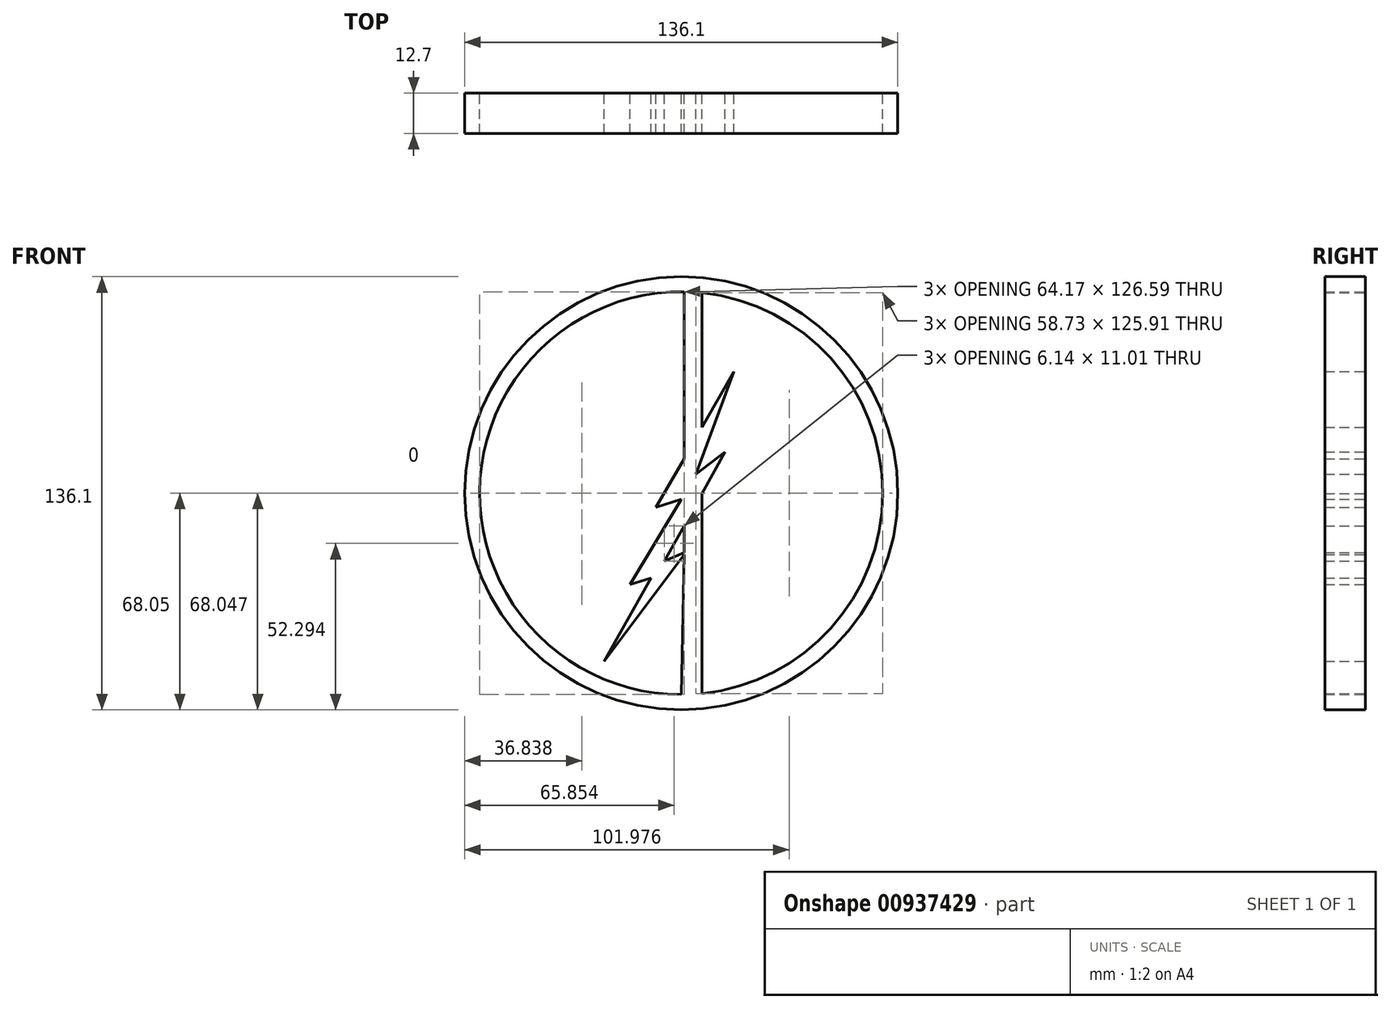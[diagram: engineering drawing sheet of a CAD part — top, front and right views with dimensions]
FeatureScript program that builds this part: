
annotation { "Feature Type Name" : "Feature", "Feature Type Description" : "" }
export const myFeature = defineFeature(function(context is Context, id is Id, definition is map)
    precondition{}
    {
        {
            var Q0;
            Q0=qCreatedBy(makeId("Front.planeOp"),FACE);
            var sketch = newSketch(context, id + "F0", { "sketchPlane" : qUnion([Q0])});
            skLineSegment(sketch, "E0", {"start": v(12.06, 38.27) * mm, "end": v(2, 20.72) * mm});
            skLineSegment(sketch, "E1", {"start": v(-12.46, -4.48) * mm, "end": v(-4.56, -1.86) * mm});
            skLineSegment(sketch, "E2", {"start": v(-4.56, -1.86) * mm, "end": v(-20.68, -28.66) * mm});
            skLineSegment(sketch, "E3", {"start": v(-20.68, -28.66) * mm, "end": v(-14.1, -26.7) * mm});
            skLineSegment(sketch, "E4", {"start": v(-14.1, -26.7) * mm, "end": v(-28.74, -52.84) * mm});
            skLineSegment(sketch, "E5", {"start": v(-28.74, -52.84) * mm, "end": v(-3.68, -19.27) * mm});
            skLineSegment(sketch, "E6", {"start": v(-3.68, -18.72) * mm, "end": v(-9.83, -21.26) * mm});
            skLineSegment(sketch, "E7", {"start": v(-9.83, -21.26) * mm, "end": v(-3.68, -10.25) * mm});
            skLineSegment(sketch, "E8", {"start": v(9.25, 12.95) * mm, "end": v(0, 6.04) * mm});
            skLineSegment(sketch, "E9", {"start": v(0, 6.04) * mm, "end": v(12.06, 38.27) * mm});
            skCircle(sketch, "E10", {"center": v(-4.56, 0) * mm, "radius": 68.05 * mm});
            skArc(sketch, "E11", {"start": v(2, -62.96) * mm, "mid": v(58.73, 0) * mm, "end": v(2, 62.96) * mm});
            skLineSegment(sketch, "E12", {"start": v(-3.68, 63.3) * mm, "end": v(-3.68, 10.82) * mm});
            skLineSegment(sketch, "E13", {"start": v(2, 62.96) * mm, "end": v(2, 20.72) * mm});
            skLineSegment(sketch, "E14", {"start": v(2, -0.07) * mm, "end": v(2, -62.96) * mm});
            skLineSegment(sketch, "E15", {"start": v(-3.68, -10.25) * mm, "end": v(-3.68, -19.27) * mm});
            skLineSegment(sketch, "E16", {"start": v(-3.68, -19.27) * mm, "end": v(-4.56, -63.3) * mm});
            skArc(sketch, "E17.trimOffspring", {"start": v(-3.68, 63.3) * mm, "mid": v(-67.86, 0.44) * mm, "end": v(-4.56, -63.3) * mm});
            skLineSegment(sketch, "E18.trimOffspring", {"start": v(-3.68, 10.82) * mm, "end": v(-12.46, -4.48) * mm});
            skLineSegment(sketch, "E19.trimOffspring", {"start": v(2, -0.07) * mm, "end": v(9.25, 12.95) * mm});
            skSolve(sketch);
        }
        {
            var Q0;
            Q0=makeQuery(id+"F0.imprint","IMPRINT",FACE,{"disambiguationData":[TD([[makeQuery(id+"F0.imprint","IMPRINT",EDGE,{"derivedFrom":sQuery(id+"F0.wireOp",EDGE,"E0")}),1.0]])]});
            extrude(context, id + "F1", {"entities" : qUnion([Q0]), "depth" : 12.7 * mm, "offsetDistance" : 25.4 * mm});
        }
        {
            var Q0;
            Q0 = qSketchRegion(id + "F0", true);
            extrude(context, id + "F2", {"entities" : qUnion([Q0]), "depth" : 12.7 * mm, "offsetDistance" : 25.4 * mm});
        }
        {
            var Q0;
            {var subQ0=sQuery(id+"F0.wireOp",EDGE,"E12");Q0=makeQuery(id+"F0.imprint","IMPRINT",FACE,{"disambiguationData":[TD([[makeQuery(id+"F0.imprint","IMPRINT",EDGE,{"derivedFrom":subQ0}),1.0]])]});}
            var Q1;
            {var subQ0=sQuery(id+"F0.wireOp",EDGE,"E14");Q1=makeQuery(id+"F0.imprint","IMPRINT",FACE,{"disambiguationData":[TD([[makeQuery(id+"F0.imprint","IMPRINT",EDGE,{"derivedFrom":subQ0}),-1.0]])]});}
            extrude(context, id + "F3", {"entities" : qUnion([Q0, Q1]), "depth" : 12.7 * mm, "offsetDistance" : 25.4 * mm});
        }
    });
